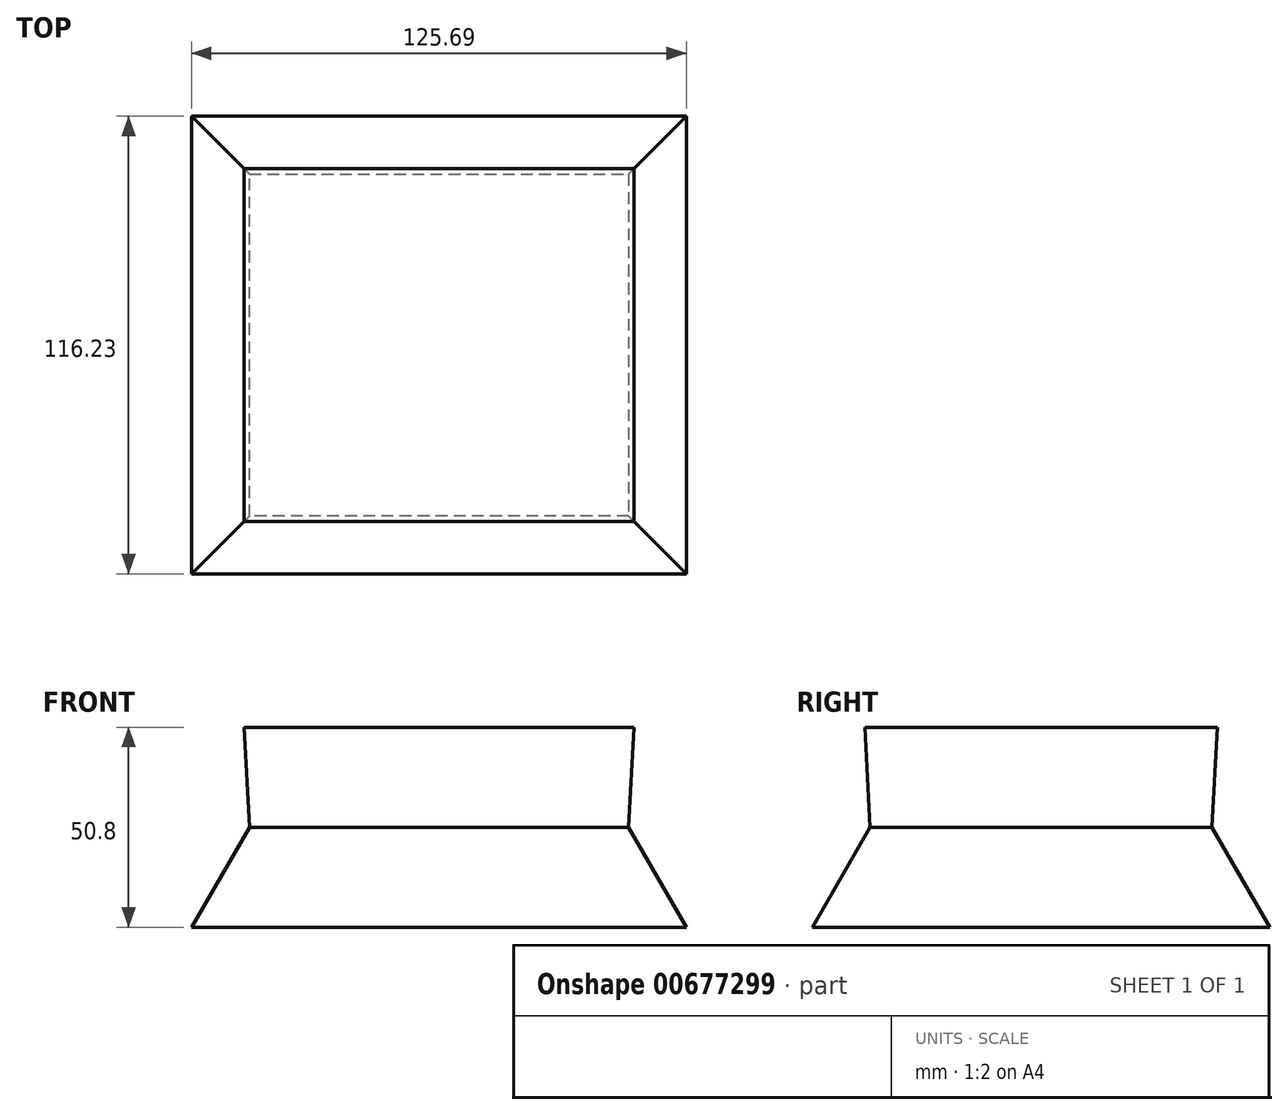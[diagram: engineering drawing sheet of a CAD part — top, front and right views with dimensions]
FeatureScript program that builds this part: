
annotation { "Feature Type Name" : "Feature", "Feature Type Description" : "" }
export const myFeature = defineFeature(function(context is Context, id is Id, definition is map)
    precondition{}
    {
        {
            var Q0;
            Q0=qCreatedBy(makeId("Top.planeOp"),FACE);
            var sketch = newSketch(context, id + "F0", { "sketchPlane" : qUnion([Q0])});
            skLineSegment(sketch, "E0.bottom", {"start": v(-103.71, 39.9) * mm, "end": v(-7.35, 39.9) * mm});
            skLineSegment(sketch, "E0.top", {"start": v(-103.71, -47) * mm, "end": v(-7.35, -47) * mm});
            skLineSegment(sketch, "E0.left", {"start": v(-103.71, 39.9) * mm, "end": v(-103.71, -47) * mm});
            skLineSegment(sketch, "E0.right", {"start": v(-7.35, 39.9) * mm, "end": v(-7.35, -47) * mm});
            skSolve(sketch);
        }
        {
            var Q0;
            Q0=makeQuery(id+"F0.imprint","IMPRINT",FACE,{"disambiguationData":[TD([[makeQuery(id+"F0.imprint","IMPRINT",EDGE,{"derivedFrom":sQuery(id+"F0.wireOp",EDGE,"E0.bottom")}),-1.0]])]});
            extrude(context, id + "F1", {"entities" : qUnion([Q0]), "depth" : 25.4 * mm, "hasDraft" : true, "draftAngle" : 3 * degree, "hasSecondDirection" : true, "secondDirectionOppositeDirection" : true, "secondDirectionDepth" : 25.4 * mm, "hasSecondDirectionDraft" : true, "secondDirectionDraftAngle" : 30 * degree});
        }
    });
